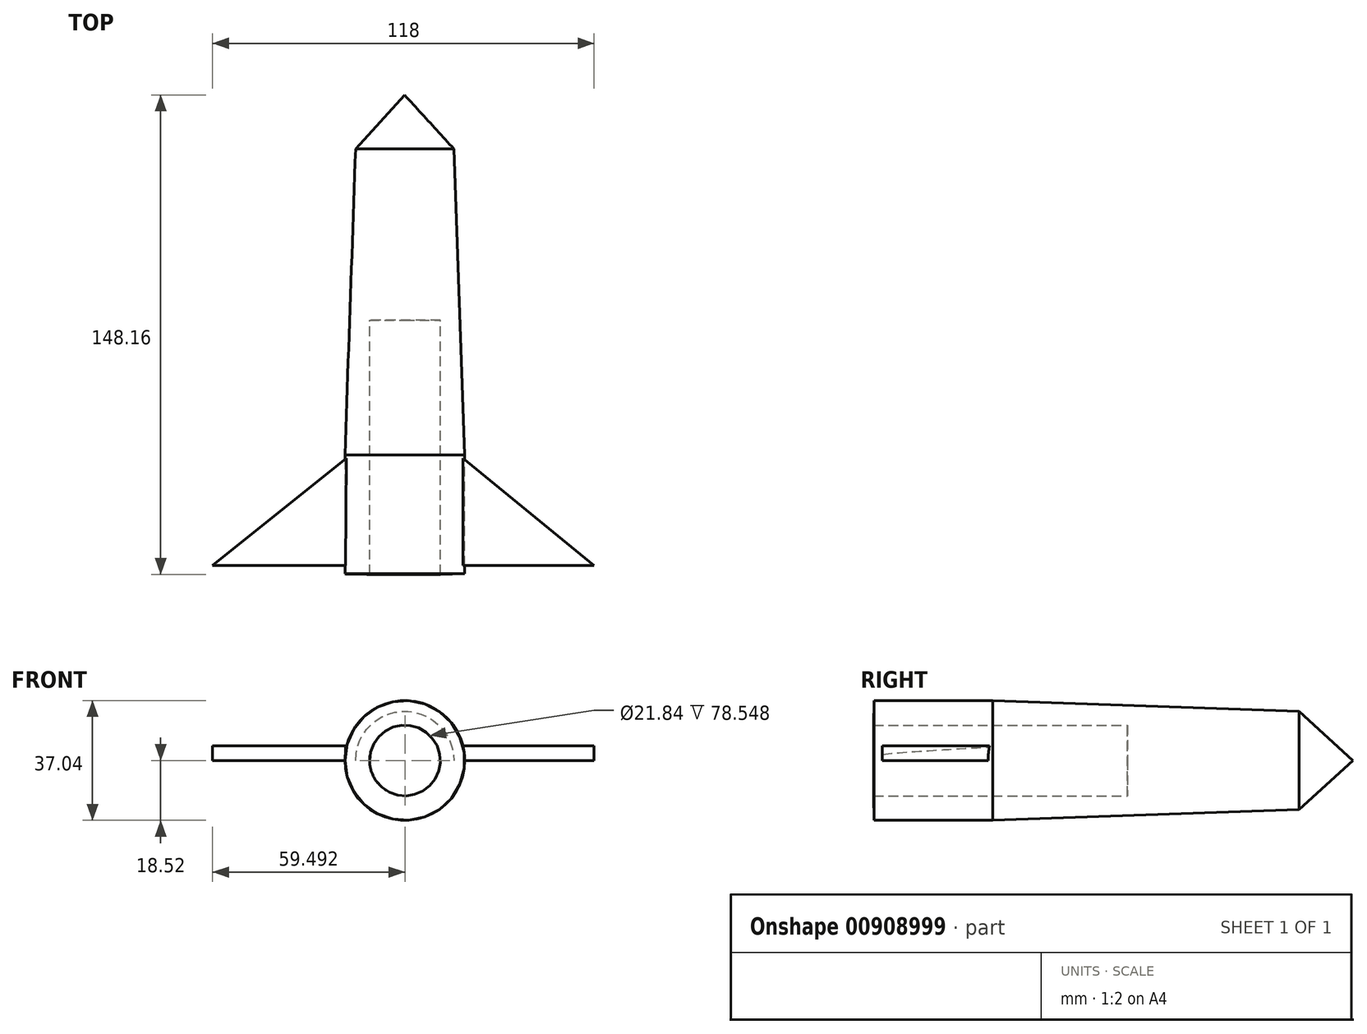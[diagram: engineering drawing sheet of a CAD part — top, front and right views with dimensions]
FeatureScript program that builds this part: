
annotation { "Feature Type Name" : "Feature", "Feature Type Description" : "" }
export const myFeature = defineFeature(function(context is Context, id is Id, definition is map)
    precondition{}
    {
        {
            var Q0;
            Q0=qCreatedBy(makeId("Top.planeOp"),FACE);
            var sketch = newSketch(context, id + "F0", { "sketchPlane" : qUnion([Q0])});
            skLineSegment(sketch, "E0", {"start": v(-34.42, 69.61) * mm, "end": v(-19.22, 52.98) * mm});
            skLineSegment(sketch, "E1", {"start": v(-19.22, 52.98) * mm, "end": v(-15.86, -41.65) * mm});
            skPoint(sketch, "E2.end.orphan", {"position": v(19.13, -78.96) * mm});
            skLineSegment(sketch, "E3", {"start": v(-15.86, -41.65) * mm, "end": v(-15.86, -78.39) * mm});
            skLineSegment(sketch, "E4", {"start": v(-34.36, -78.75) * mm, "end": v(-15.86, -78.39) * mm});
            skPoint(sketch, "E5.end.orphan", {"position": v(-34.42, -78.96) * mm});
            skLineSegment(sketch, "E6", {"start": v(-34.42, 69.61) * mm, "end": v(-34.36, -78.75) * mm});
            skSolve(sketch);
        }
        {
            var Q0;
            Q0=makeQuery(id+"F0.imprint","IMPRINT",FACE,{"disambiguationData":[TD([[makeQuery(id+"F0.imprint","IMPRINT",EDGE,{"derivedFrom":sQuery(id+"F0.wireOp",EDGE,"E0")}),-1.0]])]});
            var Q1;
            Q1=sQuery(id+"F0.wireOp",EDGE,"E6");
            revolve(context, id + "F1", {"surfaceOperationType" : NewSurfaceOperationType.NEW, "entities" : qUnion([Q0]), "axis" : qUnion([Q1]), "revolveType" : RevolveType.FULL});
        }
        {
            var Q0;
            Q0=qCreatedBy(makeId("Top.planeOp"),FACE);
            var sketch = newSketch(context, id + "F2", { "sketchPlane" : qUnion([Q0])});
            skLineSegment(sketch, "E7", {"start": v(-16.91, -42.28) * mm, "end": v(24.16, -75.86) * mm});
            skLineSegment(sketch, "E8", {"start": v(24.16, -75.86) * mm, "end": v(-16.91, -75.86) * mm});
            skPoint(sketch, "E9.MirrorCS.end.orphan", {"position": v(16, -35.6) * mm});
            skPoint(sketch, "E9.MirrorCS.start.orphan", {"position": v(24.16, -75.86) * mm});
            skLineSegment(sketch, "E10", {"start": v(-52.44, -42.68) * mm, "end": v(-93.84, -75.86) * mm});
            skLineSegment(sketch, "E11", {"start": v(246.14, -75.28) * mm, "end": v(287.2, -75.86) * mm});
            skLineSegment(sketch, "E12", {"start": v(-93.84, -75.86) * mm, "end": v(-52.77, -75.86) * mm});
            skLineSegment(sketch, "E13", {"start": v(-52.77, -75.86) * mm, "end": v(-52.44, -42.68) * mm});
            skLineSegment(sketch, "E14", {"start": v(-16.91, -42.28) * mm, "end": v(-16.91, -75.86) * mm});
            skSolve(sketch);
        }
        {
            var Q0;
            Q0=makeQuery(id+"F2.imprint","IMPRINT",FACE,{"disambiguationData":[TD([[makeQuery(id+"F2.imprint","IMPRINT",EDGE,{"derivedFrom":sQuery(id+"F2.wireOp",EDGE,"E10")}),1.0]])]});
            var Q1;
            Q1=makeQuery(id+"F2.imprint","IMPRINT",FACE,{"disambiguationData":[TD([[makeQuery(id+"F2.imprint","IMPRINT",EDGE,{"derivedFrom":sQuery(id+"F2.wireOp",EDGE,"E7")}),-1.0]])]});
            extrude(context, id + "F3", {"entities" : qUnion([Q0, Q1]), "operationType" : NewBodyOperationType.ADD, "depth" : 4.57 * mm, "offsetDistance" : 25.4 * mm});
        }
        {
            var Q0;
            Q0=qCreatedBy(makeId("Front.planeOp"),FACE);
            var sketch = newSketch(context, id + "F4", { "sketchPlane" : qUnion([Q0])});
            skPoint(sketch, "E15.center.orphan", {"position": v(-128.3, 0) * mm});
            skCircle(sketch, "E16", {"center": v(-34.35, 0) * mm, "radius": 10.92 * mm});
            skSolve(sketch);
        }
        {
            var Q0;
            Q0=qSketchRegion(id+"F4",true);
            extrude(context, id + "F5", {"entities" : qUnion([Q0]), "operationType" : NewBodyOperationType.REMOVE, "depth" : 88.4 * mm, "offsetDistance" : 25.4 * mm});
        }
    });
